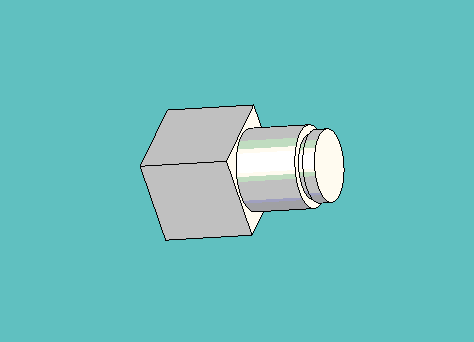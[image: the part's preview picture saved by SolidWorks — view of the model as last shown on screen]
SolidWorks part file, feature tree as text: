
SOLIDWORKS PART (.sldprt)
format: sldprt  version: not decoded by parser v0  size: 242,688 bytes
history: native  units: mm
features: sketch x3, extrude x2, material x1, revolve x1 (+11 scaffold rows collapsed)
feature tree (18):
  scaffold x11  (default folders/planes/origin — collapsed)
  material  "Material <not specified>"
  sketch  "Sketch1"  dims[D1=11.43mm D2=11.6713mm]
  extrude  "Extrude1"  Depth=5.83565mm
  sketch  "Sketch2"  dims[D1=10.4013mm]
  extrude  "Extrude2"  Depth=7.9375mm
  sketch  "Sketch3"  dims[D1=~0.79375mm D2=~2.38125mm D3=8.128mm D4=9.144mm]
  revolve  "Revolve1"  Angle=360deg
decode coverage: 6 of 6 modeling features carry decoded parameters
note: ~ marks probable driven/reference dimensions
note: suppression state not decoded; provenance and decode notes live in map.json
